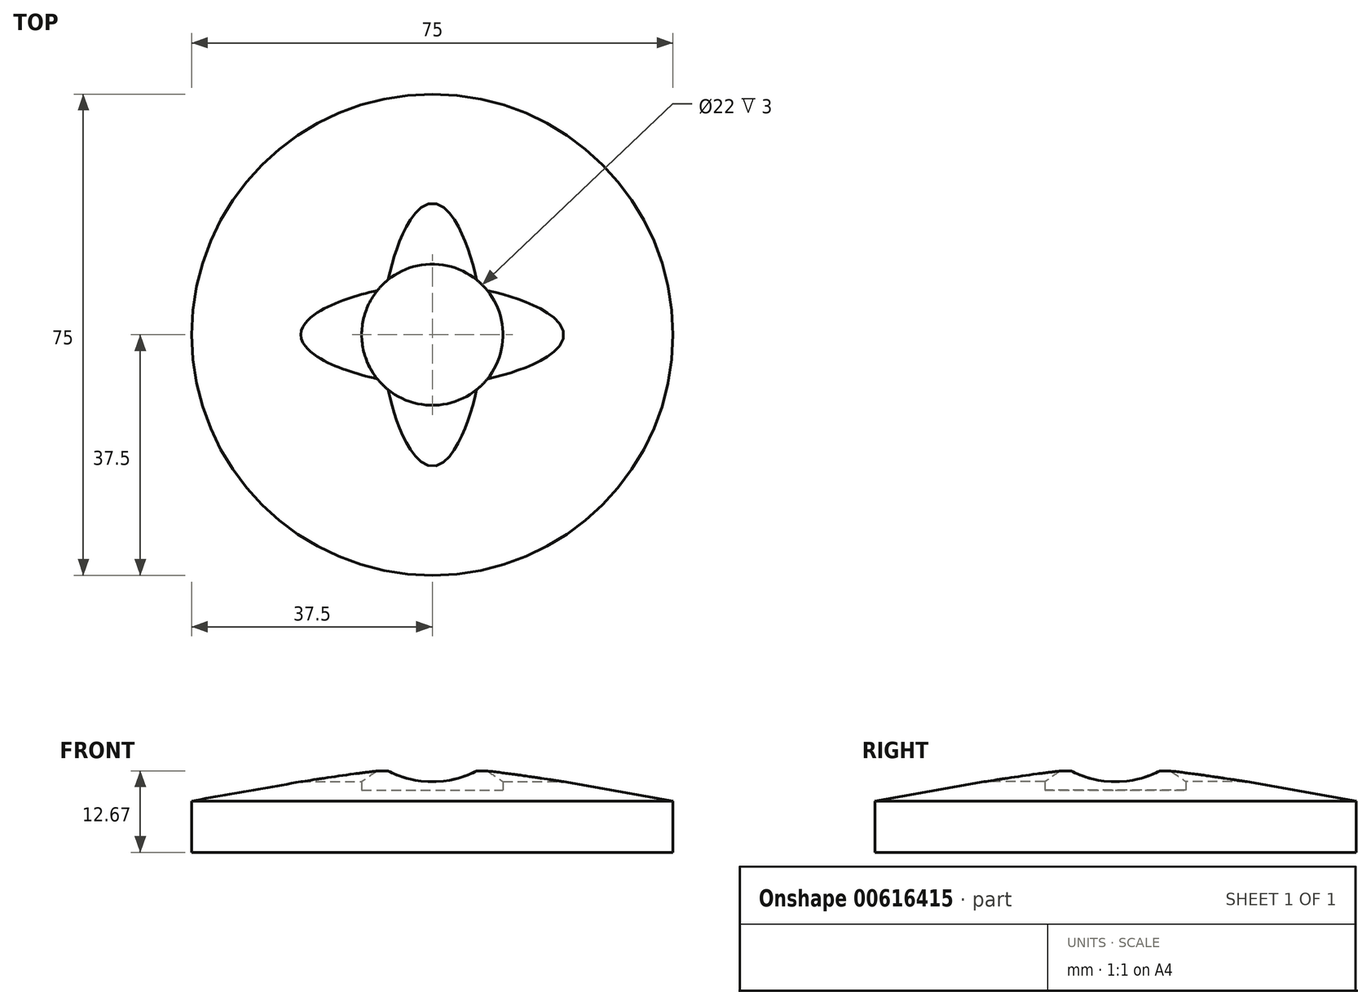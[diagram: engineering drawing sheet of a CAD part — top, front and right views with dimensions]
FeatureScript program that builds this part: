
annotation { "Feature Type Name" : "Feature", "Feature Type Description" : "" }
export const myFeature = defineFeature(function(context is Context, id is Id, definition is map)
    precondition{}
    {
        {
            var Q0;
            Q0=qCreatedBy(makeId("Front.planeOp"),FACE);
            var sketch = newSketch(context, id + "F0", { "sketchPlane" : qUnion([Q0])});
            skLineSegment(sketch, "E0", {"start": v(0, -31.7) * mm, "end": v(0, 9.67) * mm, "construction": true});
            skLineSegment(sketch, "E1.MirrorCS", {"start": v(-37.5, 0) * mm, "end": v(-37.5, 8) * mm});
            skLineSegment(sketch, "E2.MirrorCS", {"start": v(-37.5, 8) * mm, "end": v(-11, 12.67) * mm});
            skLineSegment(sketch, "E3.MirrorCS", {"start": v(0, 0) * mm, "end": v(-37.5, 0) * mm});
            skLineSegment(sketch, "E4", {"start": v(0, 0) * mm, "end": v(0, 9.67) * mm});
            skLineSegment(sketch, "E5.trimOffspring", {"start": v(0, 14.61) * mm, "end": v(0, 65.06) * mm, "construction": true});
            skLineSegment(sketch, "E6", {"start": v(-11, 12.67) * mm, "end": v(-11, 9.67) * mm});
            skLineSegment(sketch, "E7", {"start": v(-11, 9.67) * mm, "end": v(0, 9.67) * mm});
            skSolve(sketch);
        }
        {
            var Q0;
            Q0=makeQuery(id+"F0.imprint","IMPRINT",FACE,{"disambiguationData":[TD([[makeQuery(id+"F0.imprint","IMPRINT",EDGE,{"derivedFrom":sQuery(id+"F0.wireOp",EDGE,"E1.MirrorCS")}),-1.0]])]});
            var Q1;
            Q1=sQuery(id+"F0.wireOp",EDGE,"E0");
            revolve(context, id + "F1", {"entities" : qUnion([Q0]), "axis" : qUnion([Q1]), "revolveType" : RevolveType.FULL});
        }
        {
            var Q0;
            Q0=qCreatedBy(makeId("Front.planeOp"),FACE);
            var sketch = newSketch(context, id + "F2", { "sketchPlane" : qUnion([Q0])});
            skCircle(sketch, "E8", {"center": v(0, 26) * mm, "radius": 15 * mm});
            skPoint(sketch, "E9", {"position": v(0, 11) * mm});
            skSolve(sketch);
        }
        {
            var Q0;
            Q0=makeQuery(id+"F2.imprint","IMPRINT",FACE,{"disambiguationData":[TD([[makeQuery(id+"F2.imprint","IMPRINT",EDGE,{"derivedFrom":sQuery(id+"F2.wireOp",EDGE,"E8")}),1.0]])]});
            extrude(context, id + "F3", {"entities" : qUnion([Q0]), "endBound" : BoundingType.SYMMETRIC, "oppositeDirection" : true, "depth" : 80 * mm, "offsetDistance" : 25 * mm});
        }
        {
            var Q0;
            Q0=makeQuery(id+"F3.opExtrude","SWEPT_BODY",BODY,{"disambiguationData":[OSD([sQuery(id+"F2.wireOp",EDGE,"E8")])]});
            var Q1;
            Q1=sQuery(id+"F0.wireOp",EDGE,"E0");
            transform(context, id + "F4", {"entities" : qUnion([Q0]), "transformType" : TransformType.ROTATION, "transformAxis" : qUnion([Q1]), "angle" : 90 * degree, "makeCopy" : true});
        }
        {
            var Q0;
            Q0=makeQuery(id+"F3.opExtrude","SWEPT_BODY",BODY,{"disambiguationData":[OSD([sQuery(id+"F2.wireOp",EDGE,"E8")])]});
            var Q1;
            Q1=makeQuery(id+"F4.opPattern","COPY",BODY,{"derivedFrom":makeQuery(id+"F3.opExtrude","SWEPT_BODY",BODY,{"disambiguationData":[OSD([sQuery(id+"F2.wireOp",EDGE,"E8")])]}),"instanceName":"1"});
            var Q2;
            Q2=makeQuery(id+"F1.opRevolve","SWEPT_BODY",BODY,{"disambiguationData":[OSD([sQuery(id+"F0.wireOp",EDGE,"E1.MirrorCS"),sQuery(id+"F0.wireOp",EDGE,"E2.MirrorCS"),sQuery(id+"F0.wireOp",EDGE,"E3.MirrorCS"),sQuery(id+"F0.wireOp",EDGE,"E4")])]});
            booleanBodies(context, id + "F5", {"operationType" : BooleanOperationType.SUBTRACTION, "tools" : qUnion([Q0, Q1]), "targets" : qUnion([Q2])});
        }
    });
